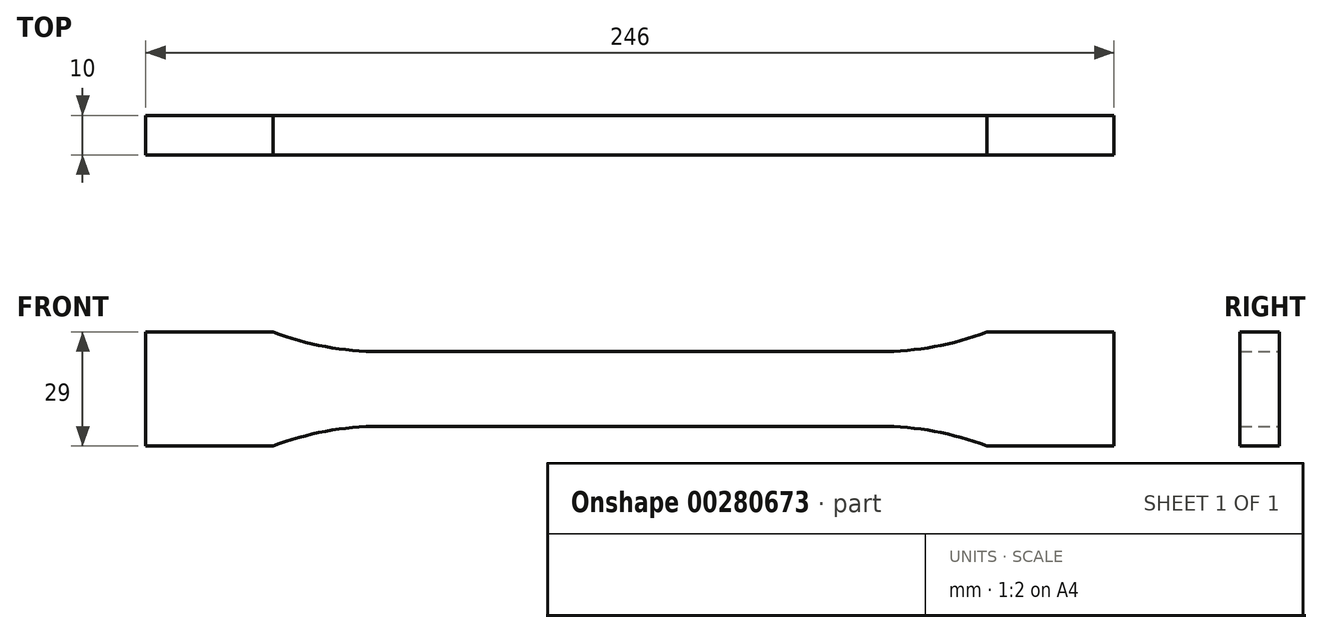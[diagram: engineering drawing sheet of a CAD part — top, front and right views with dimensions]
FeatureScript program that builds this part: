
annotation { "Feature Type Name" : "Feature", "Feature Type Description" : "" }
export const myFeature = defineFeature(function(context is Context, id is Id, definition is map)
    precondition{}
    {
        {
            var Q0;
            Q0=qCreatedBy(makeId("Front.planeOp"),FACE);
            var sketch = newSketch(context, id + "F0", { "sketchPlane" : qUnion([Q0])});
            skLineSegment(sketch, "E0", {"start": v(0, 9.5) * mm, "end": v(63.58, 9.5) * mm});
            skArc(sketch, "E1", {"start": v(63.58, 9.5) * mm, "mid": v(77.36, 10.76) * mm, "end": v(90.69, 14.5) * mm});
            skLineSegment(sketch, "E2", {"start": v(90.69, 14.5) * mm, "end": v(123, 14.5) * mm});
            skLineSegment(sketch, "E3.MirrorCS", {"start": v(90.69, -14.5) * mm, "end": v(123, -14.5) * mm});
            skLineSegment(sketch, "E4.MirrorCS", {"start": v(0, -9.5) * mm, "end": v(63.58, -9.5) * mm});
            skArc(sketch, "E5.MirrorCS", {"start": v(63.58, -9.5) * mm, "mid": v(77.36, -10.76) * mm, "end": v(90.69, -14.5) * mm});
            skArc(sketch, "E6.MirrorCS", {"start": v(-63.58, -9.5) * mm, "mid": v(-77.36, -10.76) * mm, "end": v(-90.69, -14.5) * mm});
            skLineSegment(sketch, "E7.MirrorCS", {"start": v(0, 9.5) * mm, "end": v(-63.58, 9.5) * mm});
            skArc(sketch, "E8.MirrorCS", {"start": v(-63.58, 9.5) * mm, "mid": v(-77.36, 10.76) * mm, "end": v(-90.69, 14.5) * mm});
            skLineSegment(sketch, "E9.MirrorCS", {"start": v(-90.69, -14.5) * mm, "end": v(-123, -14.5) * mm});
            skLineSegment(sketch, "E10.MirrorCS", {"start": v(0, -9.5) * mm, "end": v(-63.58, -9.5) * mm});
            skLineSegment(sketch, "E11.MirrorCS", {"start": v(-90.69, 14.5) * mm, "end": v(-123, 14.5) * mm});
            skLineSegment(sketch, "E12", {"start": v(-123, 14.5) * mm, "end": v(-123, -14.5) * mm});
            skLineSegment(sketch, "E13", {"start": v(123, 14.5) * mm, "end": v(123, -14.5) * mm});
            skSolve(sketch);
        }
        {
            var Q0;
            Q0 = qSketchRegion(id + "F0", true);
            extrude(context, id + "F1", {"entities" : qUnion([Q0]), "depth" : 10 * mm});
        }
    });
